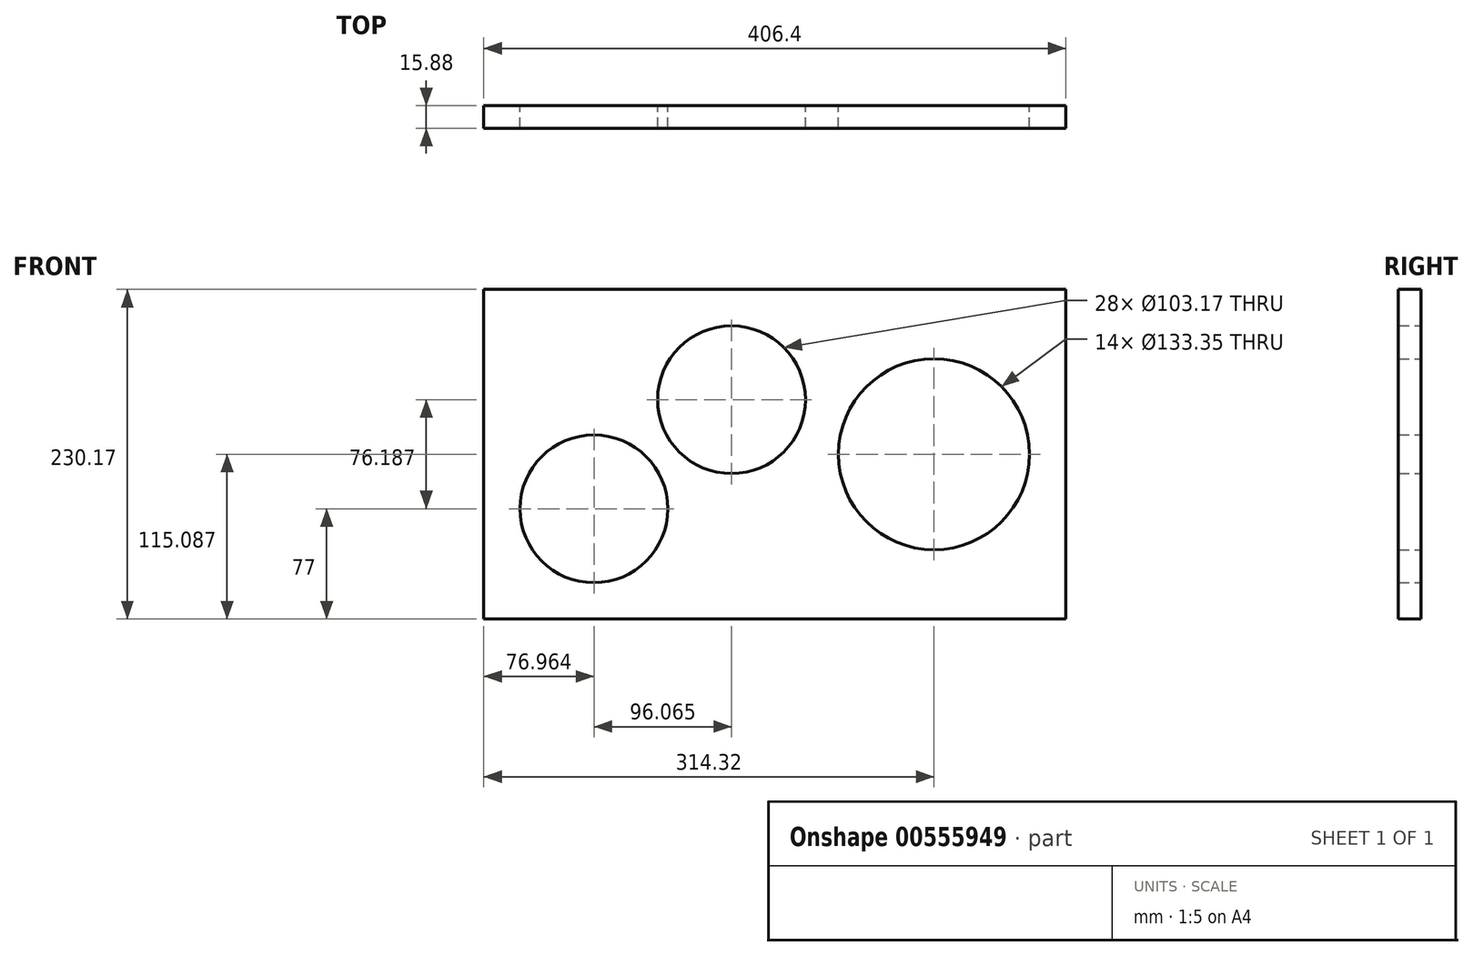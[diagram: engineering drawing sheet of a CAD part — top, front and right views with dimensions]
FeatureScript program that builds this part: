
annotation { "Feature Type Name" : "Feature", "Feature Type Description" : "" }
export const myFeature = defineFeature(function(context is Context, id is Id, definition is map)
    precondition{}
    {
        {
            var Q0;
            Q0=qCreatedBy(makeId("Front.planeOp"),FACE);
            var sketch = newSketch(context, id + "F0", { "sketchPlane" : qUnion([Q0])});
            skLineSegment(sketch, "E0", {"start": v(-113.72, 230.17) * mm, "end": v(292.68, 230.17) * mm});
            skLineSegment(sketch, "E1", {"start": v(292.68, 230.17) * mm, "end": v(292.68, 0) * mm});
            skLineSegment(sketch, "E2", {"start": v(292.68, 0) * mm, "end": v(-113.72, 0) * mm});
            skLineSegment(sketch, "E3", {"start": v(-113.72, 0) * mm, "end": v(-113.72, 230.17) * mm});
            skCircle(sketch, "E4", {"center": v(200.6, 115.09) * mm, "radius": 66.68 * mm});
            skPoint(sketch, "E5.end.orphan", {"position": v(292.68, 115.09) * mm});
            skPoint(sketch, "E6.end.orphan", {"position": v(-38.08, 77) * mm});
            skCircle(sketch, "E7", {"center": v(-36.76, 77) * mm, "radius": 51.59 * mm});
            skPoint(sketch, "E8.end.orphan", {"position": v(-164.37, 230.17) * mm});
            skPoint(sketch, "E9.orphan", {"position": v(-164.37, 153.19) * mm});
            skPoint(sketch, "E10.orphan", {"position": v(14.83, 153.19) * mm});
            skLineSegment(sketch, "E11", {"start": v(72, 153.19) * mm, "end": v(59.3, 153.19) * mm});
            skCircle(sketch, "E12", {"center": v(59.3, 153.19) * mm, "radius": 51.59 * mm});
            skSolve(sketch);
        }
        {
            var Q0;
            Q0 = qSketchRegion(id + "F0", true);
            extrude(context, id + "F1", {"entities" : qUnion([Q0]), "depth" : 15.88 * mm, "offsetDistance" : 25.4 * mm});
        }
    });
